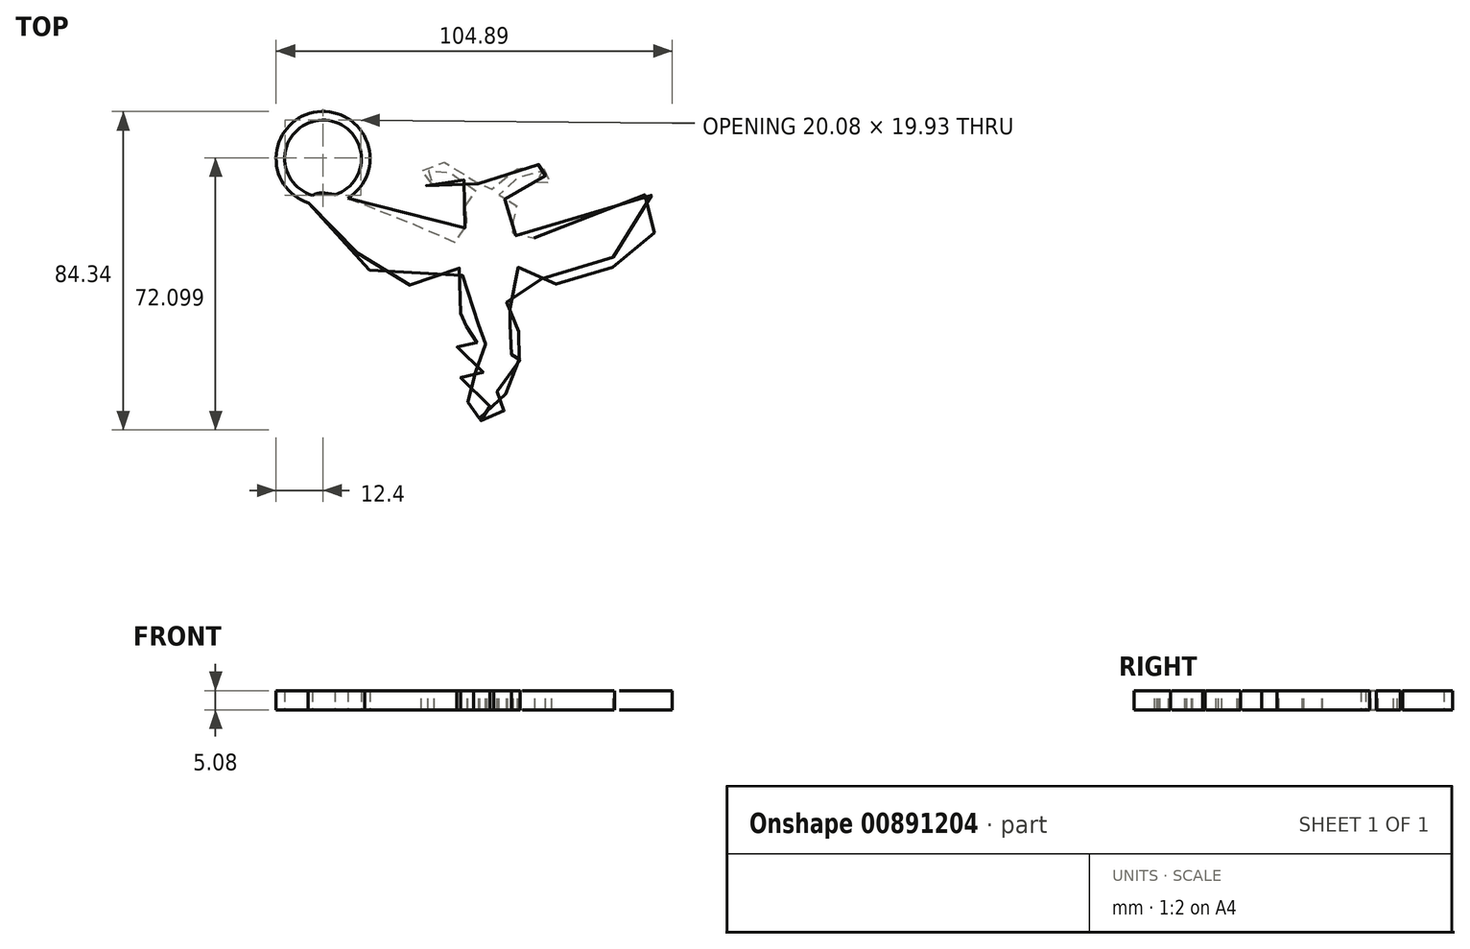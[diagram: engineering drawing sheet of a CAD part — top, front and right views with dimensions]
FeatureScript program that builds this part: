
annotation { "Feature Type Name" : "Feature", "Feature Type Description" : "" }
export const myFeature = defineFeature(function(context is Context, id is Id, definition is map)
    precondition{}
    {
        {
            var Q0;
            Q0=qCreatedBy(makeId("Top.planeOp"),FACE);
            var sketch = newSketch(context, id + "F0", { "sketchPlane" : qUnion([Q0])});
            skPoint(sketch, "E0.110.internal.snap0", {"position": v(12.5, -36.9) * mm});
            skPoint(sketch, "E0.117.internal.snap0", {"position": v(12.5, -36.9) * mm});
            skPoint(sketch, "E0.118.internal.snap0", {"position": v(12.5, -36.9) * mm});
            skFitSpline(sketch, "E0", {"points": [v(-34.8, 28) * mm, v(-29.02, 28.64) * mm, v(-11.05, 22.22) * mm, v(1.78, 16.44) * mm, v(4.03, 16.12) * mm, v(5.31, 18.69) * mm, v(6.28, 20.3) * mm, v(6.6, 21.9) * mm, v(5, 23.18) * mm, v(6.28, 25.75) * mm, v(8.52, 28) * mm, v(9.59, 28.24) * mm, v(8.35, 29.97) * mm, v(5.38, 32.7) * mm, v(1.17, 34.67) * mm, v(-1.8, 35.91) * mm, v(-3.53, 35.17) * mm, v(-3.78, 33.93) * mm, v(-3.53, 32.7) * mm, v(-2.3, 31.95) * mm, v(-2.79, 30.96) * mm, v(-4.77, 31.21) * mm, v(-5.5, 33.2) * mm, v(-5.01, 36.16) * mm, v(-2.54, 37.15) * mm, v(1.42, 36.9) * mm, v(7.11, 33.44) * mm, v(10.58, 30.22) * mm, v(11.81, 28.98) * mm, v(12.55, 29.48) * mm, v(15.28, 32.45) * mm, v(19.48, 35.17) * mm, v(21.46, 36.4) * mm, v(24.68, 36.65) * mm, v(27.9, 35.66) * mm, v(28.89, 33.93) * mm, v(28.64, 31.95) * mm, v(26.41, 30.72) * mm, v(24.68, 30.47) * mm, v(24.68, 31.7) * mm, v(26.41, 32.45) * mm, v(27.15, 33.2) * mm, v(27.15, 34.43) * mm, v(25.67, 34.92) * mm, v(23.2, 34.67) * mm, v(19.48, 32.7) * mm, v(16.02, 30.22) * mm, v(15.03, 28.98) * mm, v(15.28, 28) * mm, v(17, 27.25) * mm, v(19.24, 26.26) * mm, v(19.98, 24.03) * mm, v(19.98, 22.8) * mm, v(19.24, 21.56) * mm, v(18.25, 21.31) * mm, v(17.5, 21.06) * mm, v(17.26, 20.32) * mm, v(17.5, 19.83) * mm, v(19.24, 17.85) * mm, v(20.23, 16.86) * mm, v(20.47, 16.12) * mm, v(43.49, 25.77) * mm, v(52.64, 28.49) * mm, v(58.33, 27.75) * mm, v(60.8, 25.27) * mm, v(58.09, 20.57) * mm, v(48.68, 13.15) * mm, v(45.22, 12.16) * mm, v(45.22, 11.66) * mm, v(45.47, 10.18) * mm, v(42.25, 7.46) * mm, v(34.83, 4.24) * mm, v(32.85, 4.24) * mm, v(28.14, 5.48) * mm, v(23.2, 8.44) * mm, v(20.47, 10.67) * mm, v(19.98, 10.67) * mm, v(19.98, 9.68) * mm, v(19.73, 6.96) * mm, v(18.5, 3.5) * mm, v(17.26, 0) * mm, v(17, 0) * mm, v(18, -1.7) * mm, v(18.74, -2.44) * mm, v(17, -3.19) * mm, v(14.78, -4.92) * mm, v(14.53, -5.66) * mm, v(17, -5.9) * mm, v(19.48, -5.66) * mm, v(20.23, -7.89) * mm, v(20.47, -11.6) * mm, v(20.23, -13.08) * mm, v(17.26, -13.83) * mm, v(14.78, -14.32) * mm, v(14.78, -14.82) * mm, v(15.77, -15.56) * mm, v(19.24, -15.31) * mm, v(20.47, -15.06) * mm, v(20.23, -17.04) * mm, v(19.24, -21.5) * mm, v(18.74, -22.73) * mm, v(16.02, -23.48) * mm, v(13.8, -23.72) * mm, v(13.54, -24.22) * mm, v(14.29, -24.71) * mm, v(18, -24.22) * mm, v(17.59, -26.44) * mm, v(15.67, -29.38) * mm, v(13.9, -31.44) * mm, v(13.02, -32.91) * mm, v(12.5, -33.65) * mm, v(11.26, -33.5) * mm, v(9.93, -31) * mm, v(8.32, -28.8) * mm, v(8.32, -28.06) * mm, v(9.79, -27.76) * mm, v(11.55, -28.2) * mm, v(12.5, -28.2) * mm, v(12.5, -27.47) * mm, v(11.4, -27.03) * mm, v(9.5, -27.03) * mm, v(7.29, -27.03) * mm, v(4.79, -20.26) * mm, v(4.96, -19.82) * mm, v(5.63, -19.88) * mm, v(8.6, -20.29) * mm, v(11.3, -19.88) * mm, v(11.77, -19.21) * mm, v(11.5, -18.4) * mm, v(10.42, -18.54) * mm, v(7.52, -18.33) * mm, v(4.96, -18.06) * mm, v(4.29, -15.5) * mm, v(3.9, -11.69) * mm, v(6.39, -11.88) * mm, v(9.82, -12.07) * mm, v(10.97, -11.69) * mm, v(11.35, -10.73) * mm, v(8.49, -10.54) * mm, v(4.48, -9.59) * mm, v(4.1, -9.4) * mm, v(3.9, -8.06) * mm, v(4.1, -5.77) * mm, v(6.58, -6.34) * mm, v(8.68, -6.15) * mm, v(9.82, -5.4) * mm, v(8.49, -4.25) * mm, v(5.63, -3.48) * mm, v(4.86, -3.3) * mm, v(4.86, -1.2) * mm, v(5.45, 0) * mm, v(6.42, 1.5) * mm, v(5.77, 6) * mm, v(3.85, 10.5) * mm, v(3.53, 11.14) * mm, v(1.28, 9.2) * mm, v(-5.78, 4.72) * mm, v(-18.94, 8.25) * mm, v(-20.54, 11.78) * mm, v(-20.54, 12.42) * mm, v(-22.47, 13.06) * mm, v(-28.88, 17.55) * mm, v(-34.98, 23) * mm, v(-34.8, 28) * mm]});
            skArc(sketch, "E1", {"start": v(-25.05, 27.6) * mm, "mid": v(-33.12, 50.5) * mm, "end": v(-35.5, 26.34) * mm});
            skArc(sketch, "E2", {"start": v(-28.44, 28.5) * mm, "mid": v(-31.85, 48.3) * mm, "end": v(-34.38, 28.38) * mm});
            skSolve(sketch);
        }
        {
            var Q0;
            Q0 = qSketchRegion(id + "F0", true);
            extrude(context, id + "F1", {"entities" : qUnion([Q0]), "depth" : 5.08 * mm, "offsetDistance" : 25.4 * mm});
        }
    });
